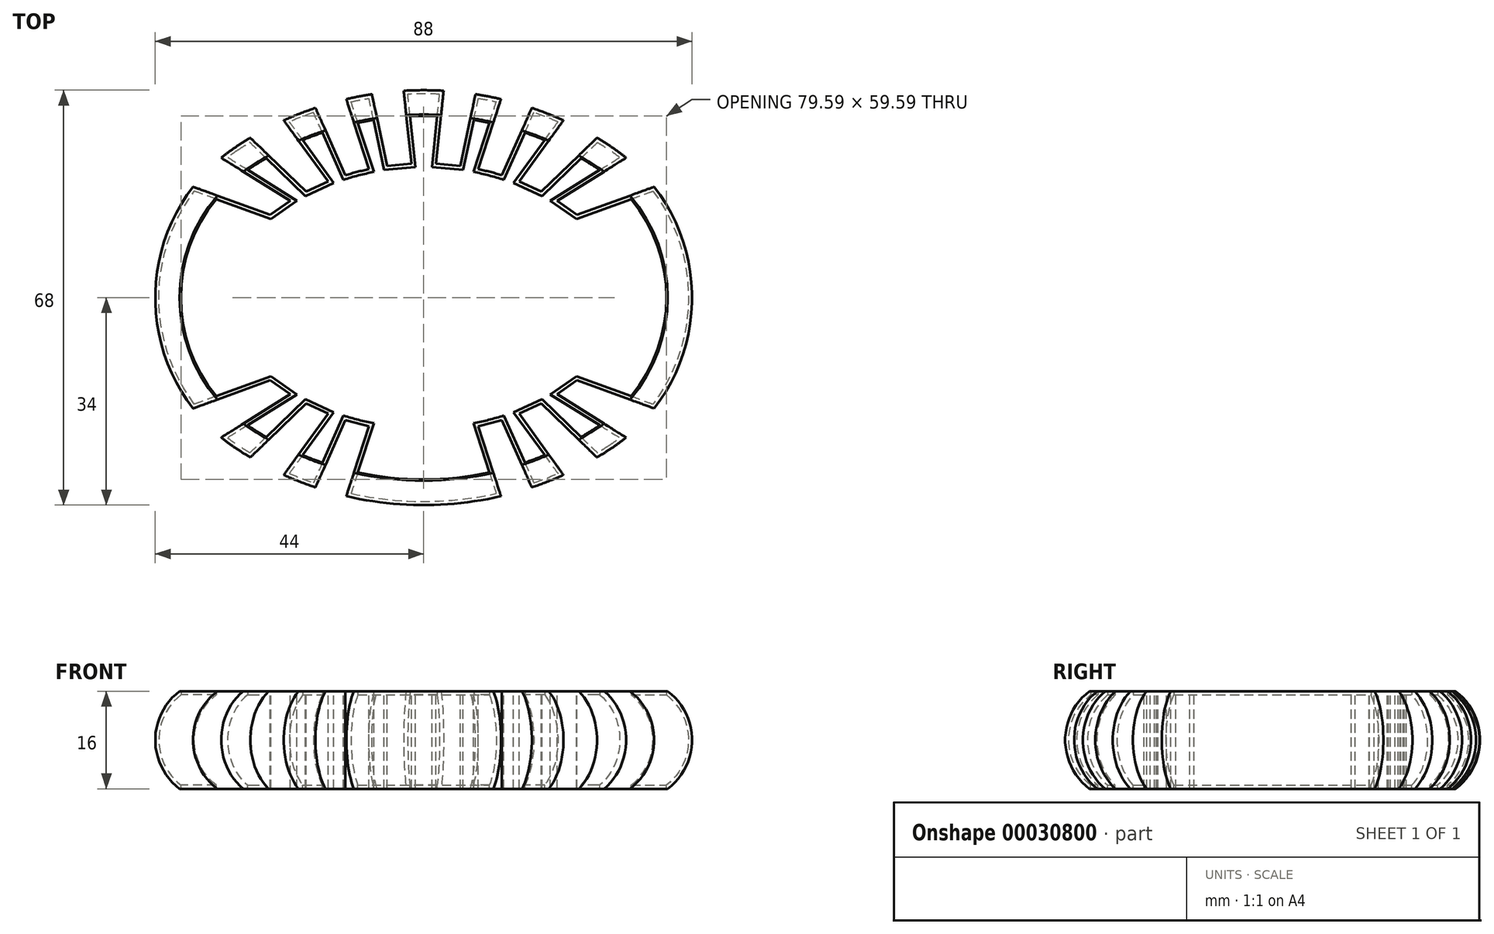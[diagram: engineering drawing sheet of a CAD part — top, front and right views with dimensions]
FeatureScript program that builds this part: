
annotation { "Feature Type Name" : "Feature", "Feature Type Description" : "" }
export const myFeature = defineFeature(function(context is Context, id is Id, definition is map)
    precondition{}
    {
        {
            var Q0;
            Q0=qCreatedBy(makeId("Top.planeOp"),FACE);
            var sketch = newSketch(context, id + "F0", { "sketchPlane" : qUnion([Q0])});
            skLineSegment(sketch, "E0.bottom", {"start": v(0, 0) * mm, "end": v(40, 0) * mm, "construction": true});
            skLineSegment(sketch, "E0.top", {"start": v(0, 30) * mm, "end": v(40, 30) * mm, "construction": true});
            skLineSegment(sketch, "E0.left", {"start": v(0, 0) * mm, "end": v(0, 30) * mm, "construction": true});
            skLineSegment(sketch, "E0.right", {"start": v(40, 0) * mm, "end": v(40, 30) * mm, "construction": true});
            skLineSegment(sketch, "E1", {"start": v(0, 0) * mm, "end": v(40, 30) * mm, "construction": true});
            skArc(sketch, "E2", {"start": v(28.52, 21.4) * mm, "mid": v(14.9, 27.8) * mm, "end": v(0, 30) * mm});
            skArc(sketch, "E3", {"start": v(40, 0) * mm, "mid": v(36.95, 12.14) * mm, "end": v(28.52, 21.4) * mm});
            skSolve(sketch);
        }
        {
            var Q0;
            Q0=qCreatedBy(makeId("Front.planeOp"),FACE);
            var sketch = newSketch(context, id + "F1", { "sketchPlane" : qUnion([Q0])});
            skArc(sketch, "E4", {"start": v(40, -16) * mm, "mid": v(44, -8) * mm, "end": v(40, 0) * mm});
            skLineSegment(sketch, "E5", {"start": v(40, 0) * mm, "end": v(30, 0) * mm});
            skLineSegment(sketch, "E6", {"start": v(30, -16) * mm, "end": v(40, -16) * mm});
            skLineSegment(sketch, "E7", {"start": v(30, 0) * mm, "end": v(30, -16) * mm});
            skSolve(sketch);
        }
        {
            var Q0;
            Q0 = qSketchRegion(id + "F1", true);
            var Q1;
            Q1=sQuery(id+"F0.wireOp",EDGE,"E3");
            var Q2;
            Q2=sQuery(id+"F0.wireOp",EDGE,"E2");
            sweep(context, id + "F2", {"profiles" : qUnion([Q0]), "path" : qUnion([Q1, Q2])});
        }
        {
            var Q0;
            Q0=makeQuery(id+"F2.opSweep","SWEPT_FACE",FACE,{"disambiguationData":[OSD([sQuery(id+"F0.wireOp",EDGE,"E3"),sQuery(id+"F1.wireOp",EDGE,"E5")])]});
            var sketch = newSketch(context, id + "F3", { "sketchPlane" : qUnion([Q0])});
            skLineSegment(sketch, "E8", {"start": v(8.95, 21.06) * mm, "end": v(13.59, 35.32) * mm});
            skLineSegment(sketch, "E9", {"start": v(13.59, 35.32) * mm, "end": v(18.92, 33.76) * mm});
            skLineSegment(sketch, "E10", {"start": v(12.82, 20.06) * mm, "end": v(18.92, 33.76) * mm});
            skLineSegment(sketch, "E11", {"start": v(8.33, 19.16) * mm, "end": v(8.95, 21.06) * mm, "construction": true});
            skLineSegment(sketch, "E12", {"start": v(12, 18.23) * mm, "end": v(12.82, 20.06) * mm, "construction": true});
            skArc(sketch, "E13", {"start": v(12.82, 20.06) * mm, "mid": v(10.9, 20.6) * mm, "end": v(8.95, 21.06) * mm});
            skLineSegment(sketch, "E14", {"start": v(8.95, 21.06) * mm, "end": v(0, 22) * mm, "construction": true});
            skLineSegment(sketch, "E15", {"start": v(0, 22) * mm, "end": v(0, 20) * mm, "construction": true});
            skLineSegment(sketch, "E16", {"start": v(15.64, 19.02) * mm, "end": v(24.46, 31.16) * mm});
            skLineSegment(sketch, "E17", {"start": v(24.46, 31.16) * mm, "end": v(30.07, 27.79) * mm});
            skLineSegment(sketch, "E18", {"start": v(30.07, 27.79) * mm, "end": v(19.28, 17.37) * mm});
            skLineSegment(sketch, "E19", {"start": v(15.64, 19.02) * mm, "end": v(19.28, 17.37) * mm});
            skLineSegment(sketch, "E20", {"start": v(15.64, 19.02) * mm, "end": v(12.82, 20.06) * mm, "construction": true});
            skLineSegment(sketch, "E21", {"start": v(15.64, 19.02) * mm, "end": v(14.46, 17.4) * mm, "construction": true});
            skLineSegment(sketch, "E22", {"start": v(19.28, 17.37) * mm, "end": v(17.84, 15.98) * mm, "construction": true});
            skLineSegment(sketch, "E23", {"start": v(21.86, 15.84) * mm, "end": v(34.58, 23.8) * mm});
            skLineSegment(sketch, "E24", {"start": v(34.58, 23.8) * mm, "end": v(39.24, 18.7) * mm});
            skLineSegment(sketch, "E25", {"start": v(39.24, 18.7) * mm, "end": v(25.15, 13.56) * mm});
            skLineSegment(sketch, "E26", {"start": v(19.28, 17.37) * mm, "end": v(21.86, 15.84) * mm, "construction": true});
            skLineSegment(sketch, "E27", {"start": v(21.86, 15.84) * mm, "end": v(25.15, 13.56) * mm});
            skLineSegment(sketch, "E28", {"start": v(21.86, 15.84) * mm, "end": v(20.17, 14.78) * mm, "construction": true});
            skLineSegment(sketch, "E29", {"start": v(25.15, 13.56) * mm, "end": v(23.27, 12.88) * mm, "construction": true});
            skSolve(sketch);
        }
        {
            var Q0;
            Q0 = qSketchRegion(id + "F3", true);
            extrude(context, id + "F4", {"entities" : qUnion([Q0]), "operationType" : NewBodyOperationType.REMOVE, "oppositeDirection" : true, "depth" : 25 * mm});
        }
        {
            var Q0;
            Q0=makeQuery(id+"F2.opSweep","SWEPT_BODY",BODY,{"disambiguationData":[OSD([sQuery(id+"F0.wireOp",EDGE,"E2"),sQuery(id+"F1.wireOp",EDGE,"E4"),sQuery(id+"F1.wireOp",EDGE,"E5"),sQuery(id+"F1.wireOp",EDGE,"E6"),sQuery(id+"F1.wireOp",EDGE,"E7")])]});
            var Q1;
            Q1=makeQuery(id+"F2.opSweep","CAP_FACE",FACE,{"disambiguationData":[OSD([sQuery(id+"F0.wireOp",VERTEX,"E3.start"),sQuery(id+"F1.wireOp",EDGE,"E4"),sQuery(id+"F1.wireOp",EDGE,"E5"),sQuery(id+"F1.wireOp",EDGE,"E6"),sQuery(id+"F1.wireOp",EDGE,"E7")])],"isStart":true});
            mirror(context, id + "F5", {"operationType" : NewBodyOperationType.ADD, "entities" : qUnion([Q0]), "mirrorPlane" : qUnion([Q1])});
        }
        {
            var Q0;
            {var subQ0=makeQuery(id+"F2.opSweep","SWEPT_FACE",FACE,{"disambiguationData":[OSD([sQuery(id+"F0.wireOp",EDGE,"E3"),sQuery(id+"F1.wireOp",EDGE,"E5")])]});Q0=makeQuery(id+"F5.boolean.opBoolean","MERGE",FACE,{"derivedFrom":[subQ0,makeQuery(id+"F5.opPattern","COPY",FACE,{"derivedFrom":subQ0,"instanceName":"1"})]});}
            var sketch = newSketch(context, id + "F6", { "sketchPlane" : qUnion([Q0])});
            skLineSegment(sketch, "E30", {"start": v(2.01, 21.95) * mm, "end": v(3.58, 36.87) * mm});
            skLineSegment(sketch, "E31", {"start": v(3.58, 36.87) * mm, "end": v(9.11, 36.25) * mm});
            skLineSegment(sketch, "E32", {"start": v(9.11, 36.25) * mm, "end": v(6, 21.58) * mm});
            skLineSegment(sketch, "E33", {"start": v(2.01, 21.95) * mm, "end": v(6, 21.58) * mm});
            skLineSegment(sketch, "E34", {"start": v(8.95, 21.06) * mm, "end": v(6, 21.58) * mm, "construction": true});
            skLineSegment(sketch, "E35", {"start": v(2.01, 21.95) * mm, "end": v(1.8, 19.96) * mm, "construction": true});
            skLineSegment(sketch, "E36", {"start": v(5.58, 19.62) * mm, "end": v(6, 21.58) * mm, "construction": true});
            skLineSegment(sketch, "E37", {"start": v(8.95, 21.06) * mm, "end": v(8.33, 19.16) * mm, "construction": true});
            skSolve(sketch);
        }
        {
            var Q0;
            Q0 = qSketchRegion(id + "F6", true);
            extrude(context, id + "F7", {"entities" : qUnion([Q0]), "operationType" : NewBodyOperationType.REMOVE, "oppositeDirection" : true, "depth" : 25 * mm});
        }
        {
            var Q0;
            {var subQ0=makeQuery(id+"F2.opSweep","SWEPT_FACE",FACE,{"disambiguationData":[OSD([sQuery(id+"F0.wireOp",EDGE,"E3"),sQuery(id+"F1.wireOp",EDGE,"E5")])]});Q0=makeQuery(id+"F5.boolean.opBoolean","MERGE",FACE,{"derivedFrom":[subQ0,makeQuery(id+"F5.opPattern","COPY",FACE,{"derivedFrom":subQ0,"instanceName":"1"})]});}
            var sketch = newSketch(context, id + "F8", { "sketchPlane" : qUnion([Q0])});
            skLineSegment(sketch, "E38", {"start": v(0, -30) * mm, "end": v(0, -40) * mm});
            skLineSegment(sketch, "E39", {"start": v(0, -40) * mm, "end": v(14.53, -38.23) * mm});
            skLineSegment(sketch, "E40", {"start": v(14.53, -38.23) * mm, "end": v(11.44, -28.72) * mm});
            skLineSegment(sketch, "E41", {"start": v(11.44, -28.72) * mm, "end": v(0, -28.72) * mm});
            skLineSegment(sketch, "E42", {"start": v(0, -28.72) * mm, "end": v(0, -30) * mm});
            skSolve(sketch);
        }
        {
            var Q0;
            Q0=makeQuery(id+"F2.opSweep","SWEPT_FACE",FACE,{"disambiguationData":[OSD([sQuery(id+"F0.wireOp",EDGE,"E2"),sQuery(id+"F1.wireOp",EDGE,"E7")])]});
            var Q1;
            Q1=makeQuery(id+"F2.opSweep","CAP_FACE",FACE,{"disambiguationData":[OSD([sQuery(id+"F0.wireOp",VERTEX,"E2.end"),sQuery(id+"F1.wireOp",EDGE,"E4"),sQuery(id+"F1.wireOp",EDGE,"E5"),sQuery(id+"F1.wireOp",EDGE,"E6"),sQuery(id+"F1.wireOp",EDGE,"E7")])],"isStart":false});
            var Q2;
            Q2=makeQuery(id+"F5.opPattern","COPY",FACE,{"derivedFrom":makeQuery(id+"F2.opSweep","SWEPT_FACE",FACE,{"disambiguationData":[OSD([sQuery(id+"F0.wireOp",EDGE,"E2"),sQuery(id+"F1.wireOp",EDGE,"E7")])]}),"instanceName":"1"});
            var Q3;
            {var subQ0=makeQuery(id+"F2.opSweep","SWEPT_FACE",FACE,{"disambiguationData":[OSD([sQuery(id+"F0.wireOp",EDGE,"E3"),sQuery(id+"F1.wireOp",EDGE,"E7")])]});Q3=makeQuery(id+"F5.boolean.opBoolean","MERGE",FACE,{"derivedFrom":[subQ0,makeQuery(id+"F5.opPattern","COPY",FACE,{"derivedFrom":subQ0,"instanceName":"1"})]});}
            var Q4;
            Q4=makeQuery(id+"FBYvHmOpp04WFdu_1.boolean.opBoolean","MERGE",FACE,{"derivedFrom":[makeQuery(id+"F5.opPattern","COPY",FACE,{"derivedFrom":makeQuery(id+"F2.opSweep","CAP_FACE",FACE,{"disambiguationData":[OSD([sQuery(id+"F0.wireOp",VERTEX,"E2.end"),sQuery(id+"F1.wireOp",EDGE,"E4"),sQuery(id+"F1.wireOp",EDGE,"E5"),sQuery(id+"F1.wireOp",EDGE,"E6"),sQuery(id+"F1.wireOp",EDGE,"E7")])],"isStart":false}),"instanceName":"1"}),makeQuery(id+"FBYvHmOpp04WFdu_1.opExtrude","SWEPT_FACE",FACE,{"disambiguationData":[OSD([sQuery(id+"FDiFgKhX0xxbfct_1.wireOp",EDGE,"9e435253-080a-4bda-86d2-1322c63ef0f4")])]})]});
            shell(context, id + "F9", {"entities" : qUnion([Q0, Q1, Q2, Q3, Q4]), "thickness" : 0.6 * mm});
        }
        {
            var Q0;
            Q0=makeQuery(id+"F9.opShell","OFFSET_FACE",FACE,{"disambiguationData":[OSD([sQuery(id+"F0.wireOp",EDGE,"E3"),sQuery(id+"F1.wireOp",EDGE,"E6"),sQuery(id+"FDiFgKhX0xxbfct_1.wireOp",EDGE,"019a990f-40be-4d17-9e3b-bb0847a60eb7"),sQuery(id+"FDiFgKhX0xxbfct_1.wireOp",EDGE,"da019b78-40bf-4daf-8744-97964edee0d3"),sQuery(id+"FDiFgKhX0xxbfct_1.wireOp",EDGE,"9e435253-080a-4bda-86d2-1322c63ef0f4"),sQuery(id+"FDiFgKhX0xxbfct_1.wireOp",EDGE,"64c3ce18-9238-4e9d-83cc-5423a1d575c6")])]});
            extrude(context, id + "F10", {"entities" : qUnion([Q0]), "operationType" : NewBodyOperationType.REMOVE, "oppositeDirection" : true, "depth" : 25 * mm});
        }
        {
            var Q0;
            Q0=makeQuery(id+"F9.opShell","OFFSET_FACE",FACE,{"disambiguationData":[OSD([sQuery(id+"F0.wireOp",EDGE,"E3"),sQuery(id+"F1.wireOp",EDGE,"E6")])]});
            var Q1;
            Q1=makeQuery(id+"F9.opShell","OFFSET_FACE",FACE,{"disambiguationData":[OSD([sQuery(id+"F0.wireOp",EDGE,"E3"),sQuery(id+"F1.wireOp",EDGE,"E5"),sQuery(id+"FDiFgKhX0xxbfct_1.wireOp",EDGE,"019a990f-40be-4d17-9e3b-bb0847a60eb7"),sQuery(id+"FDiFgKhX0xxbfct_1.wireOp",EDGE,"da019b78-40bf-4daf-8744-97964edee0d3"),sQuery(id+"FDiFgKhX0xxbfct_1.wireOp",EDGE,"9e435253-080a-4bda-86d2-1322c63ef0f4"),sQuery(id+"FDiFgKhX0xxbfct_1.wireOp",EDGE,"64c3ce18-9238-4e9d-83cc-5423a1d575c6")])]});
            extrude(context, id + "F11", {"entities" : qUnion([Q0, Q1]), "operationType" : NewBodyOperationType.REMOVE, "oppositeDirection" : true, "depth" : 25 * mm});
        }
        {
            var Q0;
            Q0=makeQuery(id+"F2.opSweep","SWEPT_BODY",BODY,{"disambiguationData":[OSD([sQuery(id+"F0.wireOp",EDGE,"E2"),sQuery(id+"F1.wireOp",EDGE,"E4"),sQuery(id+"F1.wireOp",EDGE,"E5"),sQuery(id+"F1.wireOp",EDGE,"E6"),sQuery(id+"F1.wireOp",EDGE,"E7")])]});
            var Q1;
            Q1=makeQuery(id+"F2.opSweep","CAP_FACE",FACE,{"disambiguationData":[OSD([sQuery(id+"F0.wireOp",VERTEX,"E2.end"),sQuery(id+"F1.wireOp",EDGE,"E4"),sQuery(id+"F1.wireOp",EDGE,"E5"),sQuery(id+"F1.wireOp",EDGE,"E6"),sQuery(id+"F1.wireOp",EDGE,"E7")])],"isStart":false});
            mirror(context, id + "F12", {"operationType" : NewBodyOperationType.ADD, "entities" : qUnion([Q0]), "mirrorPlane" : qUnion([Q1])});
        }
    });
